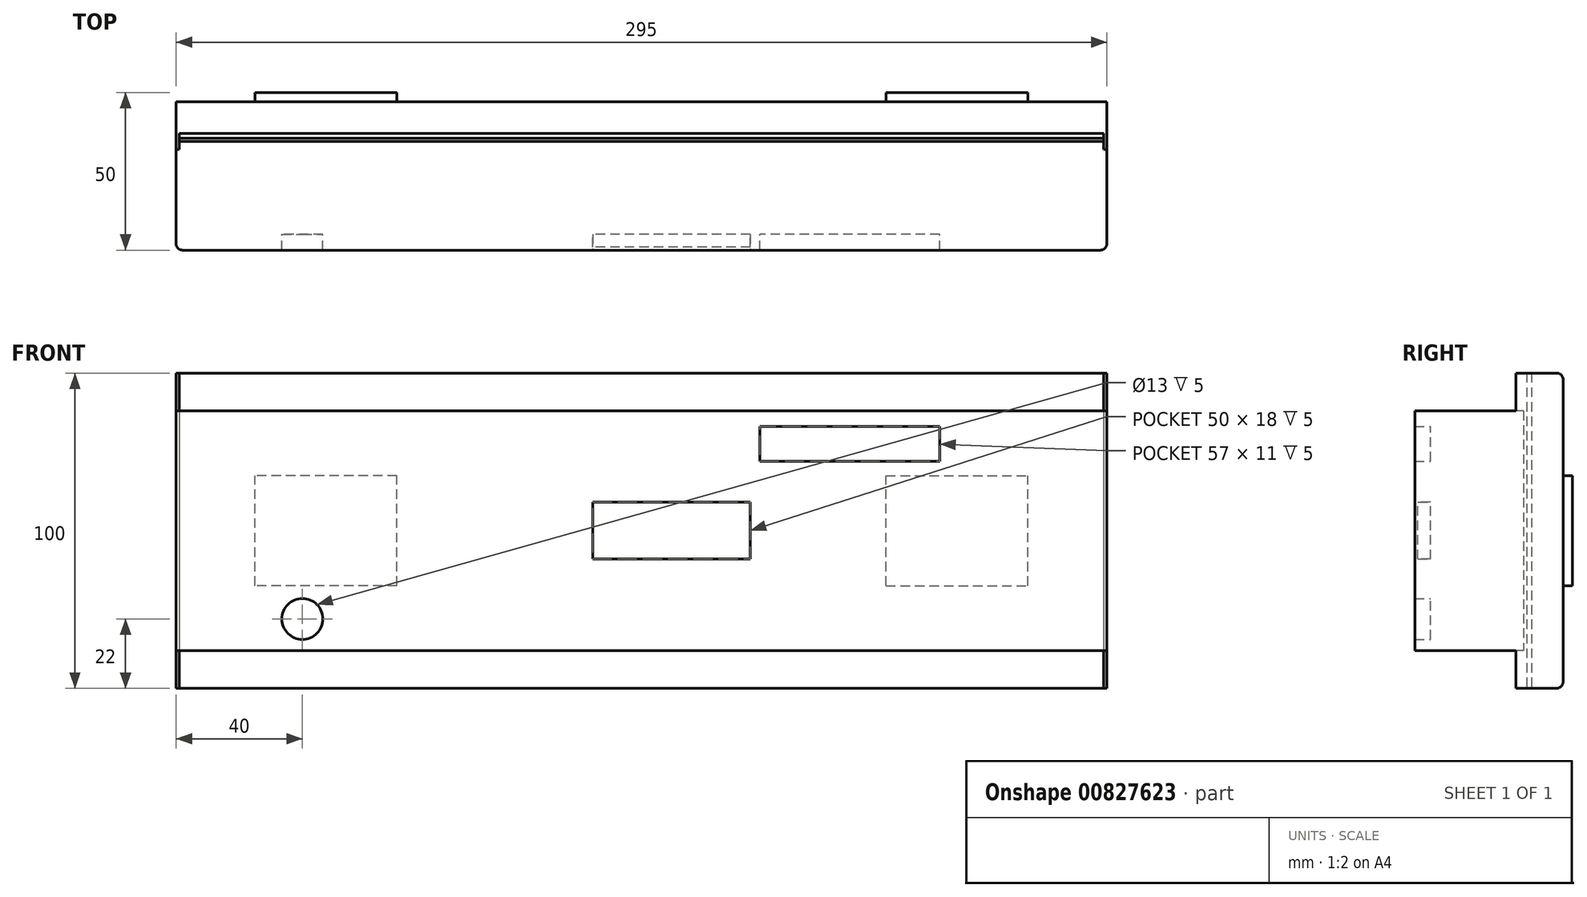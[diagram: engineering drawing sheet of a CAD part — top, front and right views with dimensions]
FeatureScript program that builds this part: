
annotation { "Feature Type Name" : "Feature", "Feature Type Description" : "" }
export const myFeature = defineFeature(function(context is Context, id is Id, definition is map)
    precondition{}
    {
        {
            var Q0;
            Q0=qCreatedBy(makeId("Front.planeOp"),FACE);
            var sketch = newSketch(context, id + "F0", { "sketchPlane" : qUnion([Q0])});
            skLineSegment(sketch, "E0.bottom", {"start": v(147.5, -50) * mm, "end": v(-147.5, -50) * mm});
            skLineSegment(sketch, "E0.top", {"start": v(147.5, 50) * mm, "end": v(-147.5, 50) * mm});
            skLineSegment(sketch, "E0.left", {"start": v(147.5, -50) * mm, "end": v(147.5, 50) * mm});
            skLineSegment(sketch, "E0.right", {"start": v(-147.5, -50) * mm, "end": v(-147.5, 50) * mm});
            skPoint(sketch, "E0.middle", {"position": v(0, 0) * mm});
            skSolve(sketch);
        }
        {
            var Q0;
            Q0=qSketchRegion(id+"F0",true);
            extrude(context, id + "F1", {"entities" : qUnion([Q0]), "depth" : 47 * mm, "offsetDistance" : 25 * mm});
        }
        {
            var Q0;
            Q0=makeQuery(id+"F1.opExtrude","CAP_FACE",FACE,{"disambiguationData":[OSD([sQuery(id+"F0.wireOp",EDGE,"E0.bottom"),sQuery(id+"F0.wireOp",EDGE,"E0.top"),sQuery(id+"F0.wireOp",EDGE,"E0.left"),sQuery(id+"F0.wireOp",EDGE,"E0.right")])],"isStart":false});
            var sketch = newSketch(context, id + "F2", { "sketchPlane" : qUnion([Q0])});
            skLineSegment(sketch, "E1.bottom", {"start": v(-147.5, -50) * mm, "end": v(147.5, -50) * mm});
            skLineSegment(sketch, "E1.top", {"start": v(-147.5, -38) * mm, "end": v(147.5, -38) * mm});
            skLineSegment(sketch, "E1.left", {"start": v(-147.5, -50) * mm, "end": v(-147.5, -38) * mm});
            skLineSegment(sketch, "E1.right", {"start": v(147.5, -50) * mm, "end": v(147.5, -38) * mm});
            skLineSegment(sketch, "E2.bottom", {"start": v(147.5, 50) * mm, "end": v(-147.5, 50) * mm});
            skLineSegment(sketch, "E2.top", {"start": v(147.5, 38) * mm, "end": v(-147.5, 38) * mm});
            skLineSegment(sketch, "E2.left", {"start": v(147.5, 50) * mm, "end": v(147.5, 38) * mm});
            skLineSegment(sketch, "E2.right", {"start": v(-147.5, 50) * mm, "end": v(-147.5, 38) * mm});
            skSolve(sketch);
        }
        {
            var Q0;
            Q0=qSketchRegion(id+"F2",true);
            extrude(context, id + "F3", {"entities" : qUnion([Q0]), "operationType" : NewBodyOperationType.REMOVE, "oppositeDirection" : true, "depth" : (47 - 15) * mm, "offsetDistance" : 25 * mm});
        }
        {
            var Q0;
            Q0=makeQuery(id+"F3.boolean.opBoolean","COPY",FACE,{"derivedFrom":makeQuery(id+"F3.opExtrude","CAP_FACE",FACE,{"disambiguationData":[OSD([sQuery(id+"F2.wireOp",EDGE,"E2.bottom"),sQuery(id+"F2.wireOp",EDGE,"E2.top"),sQuery(id+"F2.wireOp",EDGE,"E2.left"),sQuery(id+"F2.wireOp",EDGE,"E2.right")])],"isStart":false})});
            var sketch = newSketch(context, id + "F4", { "sketchPlane" : qUnion([Q0])});
            skLineSegment(sketch, "E3.bottom", {"start": v(-146.5, 50) * mm, "end": v(146.5, 50) * mm});
            skLineSegment(sketch, "E3.top", {"start": v(-146.5, 38) * mm, "end": v(146.5, 38) * mm});
            skLineSegment(sketch, "E3.left", {"start": v(-146.5, 50) * mm, "end": v(-146.5, 38) * mm});
            skLineSegment(sketch, "E3.right", {"start": v(146.5, 50) * mm, "end": v(146.5, 38) * mm});
            skSolve(sketch);
        }
        {
            var Q0;
            Q0=makeQuery(id+"F3.boolean.opBoolean","COPY",FACE,{"derivedFrom":makeQuery(id+"F3.opExtrude","CAP_FACE",FACE,{"disambiguationData":[OSD([sQuery(id+"F2.wireOp",EDGE,"E1.bottom"),sQuery(id+"F2.wireOp",EDGE,"E1.top"),sQuery(id+"F2.wireOp",EDGE,"E1.left"),sQuery(id+"F2.wireOp",EDGE,"E1.right")])],"isStart":false})});
            var sketch = newSketch(context, id + "F5", { "sketchPlane" : qUnion([Q0])});
            skLineSegment(sketch, "E4.bottom", {"start": v(-146.5, -50) * mm, "end": v(146.5, -50) * mm});
            skLineSegment(sketch, "E4.top", {"start": v(-146.5, -38) * mm, "end": v(146.5, -38) * mm});
            skLineSegment(sketch, "E4.left", {"start": v(-146.5, -50) * mm, "end": v(-146.5, -38) * mm});
            skLineSegment(sketch, "E4.right", {"start": v(146.5, -50) * mm, "end": v(146.5, -38) * mm});
            skSolve(sketch);
        }
        {
            var Q0;
            Q0=qSketchRegion(id+"F4",true);
            var Q1;
            Q1=qSketchRegion(id+"F5",true);
            extrude(context, id + "F6", {"entities" : qUnion([Q0, Q1]), "operationType" : NewBodyOperationType.REMOVE, "oppositeDirection" : true, "depth" : 5 * mm, "offsetDistance" : 25 * mm});
        }
        {
            var Q0;
            Q0=makeQuery(id+"F6.boolean.opBoolean","MERGE",FACE,{"derivedFrom":[makeQuery(id+"F3.boolean.opBoolean","COPY",FACE,{"derivedFrom":makeQuery(id+"F3.opExtrude","SWEPT_FACE",FACE,{"disambiguationData":[OSD([sQuery(id+"F2.wireOp",EDGE,"E1.top")])]})}),makeQuery(id+"F6.opExtrude","SWEPT_FACE",FACE,{"disambiguationData":[OSD([sQuery(id+"F5.wireOp",EDGE,"E4.top")])]})]});
            var sketch = newSketch(context, id + "F7", { "sketchPlane" : qUnion([Q0])});
            skLineSegment(sketch, "E5.bottom", {"start": v(-146.5, 10) * mm, "end": v(146.5, 10) * mm});
            skLineSegment(sketch, "E5.top", {"start": v(-146.5, 12.5) * mm, "end": v(146.5, 12.5) * mm});
            skLineSegment(sketch, "E5.left", {"start": v(-146.5, 10) * mm, "end": v(-146.5, 12.5) * mm});
            skLineSegment(sketch, "E5.right", {"start": v(146.5, 10) * mm, "end": v(146.5, 12.5) * mm});
            skSolve(sketch);
        }
        {
            var Q0;
            Q0=qSketchRegion(id+"F7",true);
            extrude(context, id + "F8", {"entities" : qUnion([Q0]), "operationType" : NewBodyOperationType.REMOVE, "endBound" : BoundingType.THROUGH_ALL, "oppositeDirection" : true, "depth" : 25 * mm, "offsetDistance" : 25 * mm});
        }
        {
            var Q0;
            Q0=makeQuery(id+"F1.opExtrude","CAP_FACE",FACE,{"disambiguationData":[OSD([sQuery(id+"F0.wireOp",EDGE,"E0.bottom"),sQuery(id+"F0.wireOp",EDGE,"E0.top"),sQuery(id+"F0.wireOp",EDGE,"E0.left"),sQuery(id+"F0.wireOp",EDGE,"E0.right")])],"isStart":false});
            var sketch = newSketch(context, id + "F9", { "sketchPlane" : qUnion([Q0])});
            skLineSegment(sketch, "E6.bottom", {"start": v(34.5, -9) * mm, "end": v(-15.5, -9) * mm});
            skLineSegment(sketch, "E6.top", {"start": v(34.5, 9) * mm, "end": v(-15.5, 9) * mm});
            skLineSegment(sketch, "E6.left", {"start": v(34.5, -9) * mm, "end": v(34.5, 9) * mm});
            skLineSegment(sketch, "E6.right", {"start": v(-15.5, -9) * mm, "end": v(-15.5, 9) * mm});
            skPoint(sketch, "E6.middle", {"position": v(9.5, 0) * mm});
            skCircle(sketch, "E7", {"center": v(-107.5, -28) * mm, "radius": 6.5 * mm});
            skLineSegment(sketch, "E8.bottom", {"start": v(94.5, 22) * mm, "end": v(37.5, 22) * mm});
            skLineSegment(sketch, "E8.top", {"start": v(94.5, 33) * mm, "end": v(37.5, 33) * mm});
            skLineSegment(sketch, "E8.left", {"start": v(94.5, 22) * mm, "end": v(94.5, 33) * mm});
            skLineSegment(sketch, "E8.right", {"start": v(37.5, 22) * mm, "end": v(37.5, 33) * mm});
            skPoint(sketch, "E8.middle", {"position": v(66, 27.5) * mm});
            skSolve(sketch);
        }
        {
            var Q0;
            Q0=qSketchRegion(id+"F9",true);
            extrude(context, id + "F10", {"entities" : qUnion([Q0]), "operationType" : NewBodyOperationType.REMOVE, "oppositeDirection" : true, "depth" : 5 * mm, "offsetDistance" : 25 * mm});
        }
        {
            var Q0;
            Q0=makeQuery(id+"F10.boolean.opBoolean","COPY",FACE,{"derivedFrom":makeQuery(id+"F10.opExtrude","CAP_FACE",FACE,{"disambiguationData":[OSD([sQuery(id+"F9.wireOp",EDGE,"E6.bottom"),sQuery(id+"F9.wireOp",EDGE,"E6.top"),sQuery(id+"F9.wireOp",EDGE,"E6.left"),sQuery(id+"F9.wireOp",EDGE,"E6.right")])],"isStart":false})});
            extrude(context, id + "F11", {"entities" : qUnion([Q0]), "depth" : 4 * mm, "offsetDistance" : 25 * mm});
        }
        {
            var Q0;
            Q0=makeQuery(id+"F10.boolean.opBoolean","COPY",FACE,{"derivedFrom":makeQuery(id+"F10.opExtrude","CAP_FACE",FACE,{"disambiguationData":[OSD([sQuery(id+"F9.wireOp",EDGE,"E7")])],"isStart":false})});
            var Q1;
            Q1=makeQuery(id+"F10.boolean.opBoolean","COPY",FACE,{"derivedFrom":makeQuery(id+"F10.opExtrude","CAP_FACE",FACE,{"disambiguationData":[OSD([sQuery(id+"F9.wireOp",EDGE,"E8.bottom"),sQuery(id+"F9.wireOp",EDGE,"E8.top"),sQuery(id+"F9.wireOp",EDGE,"E8.left"),sQuery(id+"F9.wireOp",EDGE,"E8.right")])],"isStart":false})});
            var Q2;
            Q2=makeQuery(id+"F1.opExtrude","CAP_FACE",FACE,{"disambiguationData":[OSD([sQuery(id+"F0.wireOp",EDGE,"E0.bottom"),sQuery(id+"F0.wireOp",EDGE,"E0.top"),sQuery(id+"F0.wireOp",EDGE,"E0.left"),sQuery(id+"F0.wireOp",EDGE,"E0.right")])],"isStart":false});
            extrude(context, id + "F12", {"entities" : qUnion([Q0, Q1]), "endBound" : BoundingType.UP_TO_SURFACE, "depth" : 25 * mm, "endBoundEntityFace" : qUnion([Q2]), "offsetDistance" : 25 * mm});
        }
        {
            var Q0;
            Q0=makeQuery(id+"F8.boolean.opBoolean","MERGE",FACE,{"derivedFrom":[makeQuery(id+"F6.boolean.opBoolean","COPY",FACE,{"derivedFrom":makeQuery(id+"F6.opExtrude","CAP_FACE",FACE,{"disambiguationData":[OSD([sQuery(id+"F4.wireOp",EDGE,"E3.bottom"),sQuery(id+"F4.wireOp",EDGE,"E3.top"),sQuery(id+"F4.wireOp",EDGE,"E3.left"),sQuery(id+"F4.wireOp",EDGE,"E3.right")])],"isStart":false})}),makeQuery(id+"F6.boolean.opBoolean","COPY",FACE,{"derivedFrom":makeQuery(id+"F6.opExtrude","CAP_FACE",FACE,{"disambiguationData":[OSD([sQuery(id+"F5.wireOp",EDGE,"E4.bottom"),sQuery(id+"F5.wireOp",EDGE,"E4.top"),sQuery(id+"F5.wireOp",EDGE,"E4.left"),sQuery(id+"F5.wireOp",EDGE,"E4.right")])],"isStart":false})}),makeQuery(id+"F8.opExtrude","SWEPT_FACE",FACE,{"disambiguationData":[OSD([sQuery(id+"F7.wireOp",EDGE,"E5.bottom")])]})]});
            extrude(context, id + "F13", {"entities" : qUnion([Q0]), "depth" : 1.5 * mm, "offsetDistance" : 25 * mm});
        }
        {
            var Q0;
            Q0=makeQuery(id+"F1.opExtrude","CAP_FACE",FACE,{"disambiguationData":[OSD([sQuery(id+"F0.wireOp",EDGE,"E0.bottom"),sQuery(id+"F0.wireOp",EDGE,"E0.top"),sQuery(id+"F0.wireOp",EDGE,"E0.left"),sQuery(id+"F0.wireOp",EDGE,"E0.right")])],"isStart":true});
            var sketch = newSketch(context, id + "F14", { "sketchPlane" : qUnion([Q0])});
            skLineSegment(sketch, "E9.bottom", {"start": v(-77.5, -17.5) * mm, "end": v(-122.5, -17.5) * mm});
            skLineSegment(sketch, "E9.top", {"start": v(-77.5, 17.5) * mm, "end": v(-122.5, 17.5) * mm});
            skLineSegment(sketch, "E9.left", {"start": v(-77.5, -17.5) * mm, "end": v(-77.5, 17.5) * mm});
            skLineSegment(sketch, "E9.right", {"start": v(-122.5, -17.5) * mm, "end": v(-122.5, 17.5) * mm});
            skPoint(sketch, "E9.middle", {"position": v(-100, 0) * mm});
            skLineSegment(sketch, "E10.bottom", {"start": v(77.5, -17.5) * mm, "end": v(122.5, -17.5) * mm});
            skLineSegment(sketch, "E10.top", {"start": v(77.5, 17.5) * mm, "end": v(122.5, 17.5) * mm});
            skLineSegment(sketch, "E10.left", {"start": v(77.5, -17.5) * mm, "end": v(77.5, 17.5) * mm});
            skLineSegment(sketch, "E10.right", {"start": v(122.5, -17.5) * mm, "end": v(122.5, 17.5) * mm});
            skPoint(sketch, "E10.middle", {"position": v(100, 0) * mm});
            skSolve(sketch);
        }
        {
            var Q0;
            Q0=qSketchRegion(id+"F14",true);
            extrude(context, id + "F15", {"entities" : qUnion([Q0]), "operationType" : NewBodyOperationType.ADD, "depth" : 3 * mm, "offsetDistance" : 25 * mm});
        }
        {
            var Q0;
            Q0=makeQuery(id+"F3.boolean.opBoolean","COPY",EDGE,{"derivedFrom":makeQuery(id+"F3.opExtrude","CAP_EDGE",EDGE,{"disambiguationData":[OSD([sQuery(id+"F2.wireOp",EDGE,"E2.top")])],"isStart":true})});
            var Q1;
            Q1=makeQuery(id+"F1.opExtrude","CAP_EDGE",EDGE,{"disambiguationData":[OSD([sQuery(id+"F0.wireOp",EDGE,"E0.left")])],"isStart":false});
            var Q2;
            Q2=makeQuery(id+"F1.opExtrude","CAP_EDGE",EDGE,{"disambiguationData":[OSD([sQuery(id+"F0.wireOp",EDGE,"E0.right")])],"isStart":false});
            var Q3;
            Q3=makeQuery(id+"F3.boolean.opBoolean","COPY",EDGE,{"derivedFrom":makeQuery(id+"F3.opExtrude","CAP_EDGE",EDGE,{"disambiguationData":[OSD([sQuery(id+"F2.wireOp",EDGE,"E1.top")])],"isStart":true})});
            var Q4;
            Q4=makeQuery(id+"F1.opExtrude","CAP_EDGE",EDGE,{"disambiguationData":[OSD([sQuery(id+"F0.wireOp",EDGE,"E0.top")])],"isStart":true});
            var Q5;
            Q5=makeQuery(id+"F1.opExtrude","CAP_EDGE",EDGE,{"disambiguationData":[OSD([sQuery(id+"F0.wireOp",EDGE,"E0.bottom")])],"isStart":true});
            fillet(context, id + "F16", {"entities" : qUnion([Q0, Q1, Q2, Q3, Q4, Q5]), "radius" : 2 * mm, "tangentPropagation" : true, "allowEdgeOverflow" : false});
        }
    });
